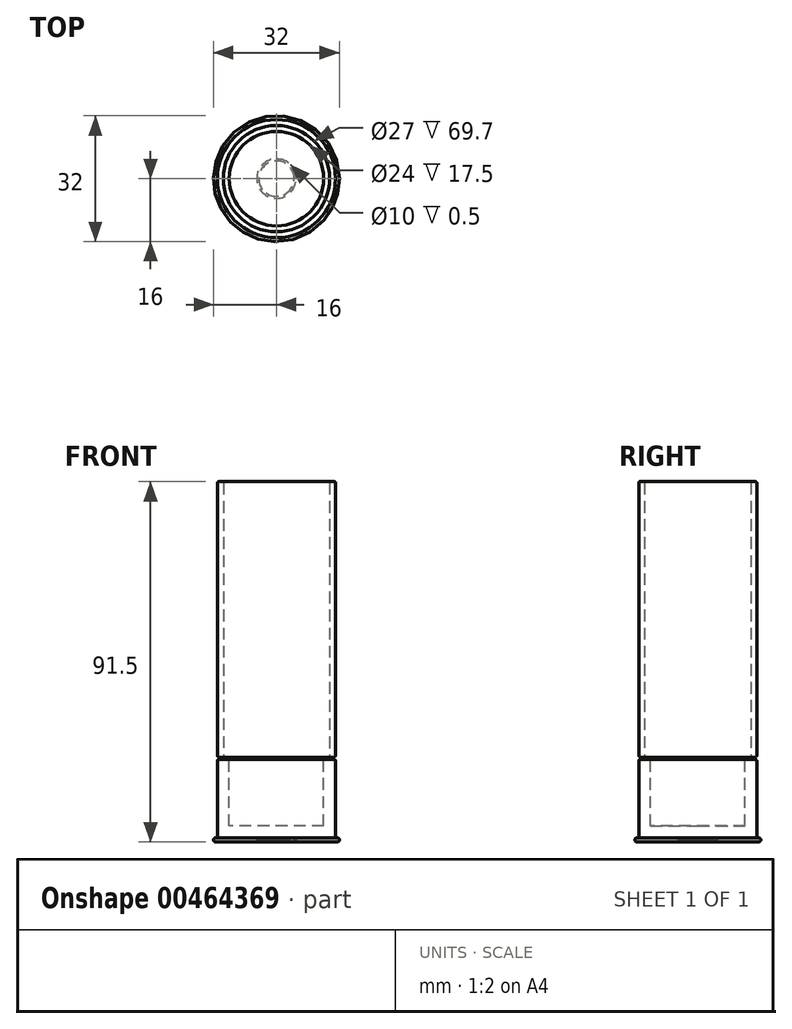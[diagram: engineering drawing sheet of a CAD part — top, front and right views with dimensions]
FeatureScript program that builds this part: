
annotation { "Feature Type Name" : "Feature", "Feature Type Description" : "" }
export const myFeature = defineFeature(function(context is Context, id is Id, definition is map)
    precondition{}
    {
        {
            var Q0;
            Q0=qCreatedBy(makeId("Top.planeOp"),FACE);
            var sketch = newSketch(context, id + "F0", { "sketchPlane" : qUnion([Q0])});
            skCircle(sketch, "E0", {"center": v(0, 0) * mm, "radius": 16 * mm});
            skSolve(sketch);
        }
        {
            var Q0;
            Q0 = qSketchRegion(id + "F0", true);
            extrude(context, id + "F1", {"entities" : qUnion([Q0]), "depth" : 1 * mm});
        }
        {
            var Q0;
            Q0=makeQuery(id+"F1.opExtrude","CAP_FACE",FACE,{"disambiguationData":[OSD([sQuery(id+"F0.wireOp",EDGE,"E0")])],"isStart":false});
            var sketch = newSketch(context, id + "F2", { "sketchPlane" : qUnion([Q0])});
            skCircle(sketch, "E1", {"center": v(0, 0) * mm, "radius": 15 * mm});
            skSolve(sketch);
        }
        {
            var Q0;
            Q0 = qSketchRegion(id + "F2", true);
            extrude(context, id + "F3", {"entities" : qUnion([Q0]), "operationType" : NewBodyOperationType.ADD, "depth" : 20 * mm});
        }
        {
            var Q0;
            Q0=makeQuery(id+"F3.opExtrude","CAP_FACE",FACE,{"disambiguationData":[OSD([sQuery(id+"F2.wireOp",EDGE,"E1")])],"isStart":false});
            var sketch = newSketch(context, id + "F4", { "sketchPlane" : qUnion([Q0])});
            skCircle(sketch, "E2", {"center": v(0, 0) * mm, "radius": 12 * mm});
            skSolve(sketch);
        }
        {
            var Q0;
            Q0 = qSketchRegion(id + "F4", true);
            extrude(context, id + "F5", {"entities" : qUnion([Q0]), "operationType" : NewBodyOperationType.REMOVE, "oppositeDirection" : true, "depth" : 17 * mm});
        }
        {
            var Q0;
            Q0=makeQuery(id+"F3.opExtrude","CAP_FACE",FACE,{"disambiguationData":[OSD([sQuery(id+"F2.wireOp",EDGE,"E1")])],"isStart":false});
            var sketch = newSketch(context, id + "F6", { "sketchPlane" : qUnion([Q0])});
            skCircle(sketch, "E3", {"center": v(0, 0) * mm, "radius": 13.5 * mm});
            skCircle(sketch, "E4", {"center": v(0, 0) * mm, "radius": 12 * mm});
            skSolve(sketch);
        }
        {
            var Q0;
            Q0 = qSketchRegion(id + "F6", true);
            extrude(context, id + "F7", {"entities" : qUnion([Q0]), "operationType" : NewBodyOperationType.ADD, "depth" : .5 * mm});
        }
        {
            var Q0;
            Q0=makeQuery(id+"F7.opExtrude","CAP_FACE",FACE,{"disambiguationData":[OSD([sQuery(id+"F6.wireOp",EDGE,"E3"),sQuery(id+"F6.wireOp",EDGE,"E4")])],"isStart":false});
            var sketch = newSketch(context, id + "F8", { "sketchPlane" : qUnion([Q0])});
            skCircle(sketch, "E5", {"center": v(0, 0) * mm, "radius": 15 * mm});
            skCircle(sketch, "E6", {"center": v(0, 0) * mm, "radius": 13.5 * mm});
            skSolve(sketch);
        }
        {
            var Q0;
            Q0 = qSketchRegion(id + "F8", true);
            extrude(context, id + "F9", {"entities" : qUnion([Q0]), "depth" : 70 * mm});
        }
        {
            var Q0;
            Q0=makeQuery(id+"F9.opExtrude","CAP_EDGE",EDGE,{"disambiguationData":[OSD([sQuery(id+"F8.wireOp",EDGE,"E5")])],"isStart":true});
            var Q1;
            Q1=makeQuery(id+"F3.opExtrude","CAP_EDGE",EDGE,{"disambiguationData":[OSD([sQuery(id+"F2.wireOp",EDGE,"E1")])],"isStart":false});
            fillet(context, id + "F10", {"entities" : qUnion([Q0, Q1]), "radius" : .5 * mm, "tangentPropagation" : true, "allowEdgeOverflow" : false});
        }
        {
            var Q0;
            Q0=makeQuery(id+"F1.opExtrude","CAP_EDGE",EDGE,{"disambiguationData":[OSD([sQuery(id+"F0.wireOp",EDGE,"E0")])],"isStart":false});
            var Q1;
            Q1=makeQuery(id+"F1.opExtrude","CAP_EDGE",EDGE,{"disambiguationData":[OSD([sQuery(id+"F0.wireOp",EDGE,"E0")])],"isStart":true});
            fillet(context, id + "F11", {"entities" : qUnion([Q0, Q1]), "radius" : .5 * mm, "tangentPropagation" : true, "allowEdgeOverflow" : false});
        }
        {
            var Q0;
            Q0=makeQuery(id+"F9.opExtrude","CAP_EDGE",EDGE,{"disambiguationData":[OSD([sQuery(id+"F8.wireOp",EDGE,"E6")])],"isStart":false});
            var Q1;
            Q1=makeQuery(id+"F9.opExtrude","CAP_EDGE",EDGE,{"disambiguationData":[OSD([sQuery(id+"F8.wireOp",EDGE,"E5")])],"isStart":false});
            fillet(context, id + "F12", {"entities" : qUnion([Q0, Q1]), "radius" : .3 * mm, "tangentPropagation" : true, "allowEdgeOverflow" : false});
        }
        {
            var Q0;
            Q0=makeQuery(id+"F1.opExtrude","CAP_FACE",FACE,{"disambiguationData":[OSD([sQuery(id+"F0.wireOp",EDGE,"E0")])],"isStart":true});
            var sketch = newSketch(context, id + "F13", { "sketchPlane" : qUnion([Q0])});
            skCircle(sketch, "E7", {"center": v(0, 0) * mm, "radius": 5 * mm});
            skCircle(sketch, "E8", {"center": v(0, 0) * mm, "radius": 4.5 * mm});
            skCircle(sketch, "E9", {"center": v(0, 0) * mm, "radius": 3.5 * mm});
            skCircle(sketch, "E10", {"center": v(0, 0) * mm, "radius": 2.5 * mm});
            skSolve(sketch);
        }
        {
            var Q0;
            Q0 = qSketchRegion(id + "F13", true);
            var Q1;
            Q1=makeQuery(id+"F13.imprint","IMPRINT",FACE,{"disambiguationData":[TD([[makeQuery(id+"F13.imprint","IMPRINT",EDGE,{"derivedFrom":sQuery(id+"F13.wireOp",EDGE,"E9")}),1.0]])]});
            extrude(context, id + "F14", {"entities" : qUnion([Q0, Q1]), "operationType" : NewBodyOperationType.REMOVE, "oppositeDirection" : true, "depth" : .5 * mm});
        }
        {
            var Q0;
            Q0=makeQuery(id+"F14.boolean.opBoolean","COPY",EDGE,{"derivedFrom":makeQuery(id+"F14.opExtrude","CAP_EDGE",EDGE,{"disambiguationData":[OSD([sQuery(id+"F13.wireOp",EDGE,"E9")])],"isStart":true})});
            var Q1;
            Q1=makeQuery(id+"F14.boolean.opBoolean","COPY",EDGE,{"derivedFrom":makeQuery(id+"F14.opExtrude","CAP_EDGE",EDGE,{"disambiguationData":[OSD([sQuery(id+"F13.wireOp",EDGE,"E7")])],"isStart":true})});
            fillet(context, id + "F15", {"entities" : qUnion([Q0, Q1]), "radius" : .5 * mm, "tangentPropagation" : true, "allowEdgeOverflow" : false});
        }
        {
            var Q0;
            Q0=makeQuery(id+"F14.boolean.opBoolean","COPY",EDGE,{"derivedFrom":makeQuery(id+"F14.opExtrude","CAP_EDGE",EDGE,{"disambiguationData":[OSD([sQuery(id+"F13.wireOp",EDGE,"E8")])],"isStart":true})});
            fillet(context, id + "F16", {"entities" : qUnion([Q0]), "radius" : .1 * mm, "tangentPropagation" : true, "allowEdgeOverflow" : false});
        }
        {
            var Q0;
            Q0=makeQuery(id+"F14.boolean.opBoolean","COPY",EDGE,{"derivedFrom":makeQuery(id+"F14.opExtrude","CAP_EDGE",EDGE,{"disambiguationData":[OSD([sQuery(id+"F13.wireOp",EDGE,"E10")])],"isStart":true})});
            fillet(context, id + "F17", {"entities" : qUnion([Q0]), "radius" : .9 * mm, "tangentPropagation" : true, "allowEdgeOverflow" : false});
        }
        {
            var Q0;
            {var subQ0=sQuery(id+"F13.wireOp",EDGE,"E9");Q0=makeQuery(id+"F15.opFillet","BLEND_EDGE",EDGE,{"blendedFrom":[makeQuery(id+"F14.boolean.opBoolean","COPY",EDGE,{"derivedFrom":makeQuery(id+"F14.opExtrude","CAP_EDGE",EDGE,{"disambiguationData":[OSD([subQ0])],"isStart":true})}),makeQuery(id+"F14.boolean.opBoolean","COPY",FACE,{"derivedFrom":makeQuery(id+"F14.opExtrude","CAP_FACE",FACE,{"disambiguationData":[OSD([subQ0,sQuery(id+"F13.wireOp",EDGE,"E10")])],"isStart":false})})],"blendedInto":[makeQuery(id+"F14.boolean.opBoolean","COPY",FACE,{"derivedFrom":makeQuery(id+"F14.opExtrude","CAP_FACE",FACE,{"disambiguationData":[OSD([subQ0,sQuery(id+"F13.wireOp",EDGE,"E10")])],"isStart":false})})]});}
            var Q1;
            {var subQ0=sQuery(id+"F13.wireOp",EDGE,"E10");Q1=makeQuery(id+"F17.opFillet","BLEND_EDGE",EDGE,{"blendedFrom":[makeQuery(id+"F14.boolean.opBoolean","COPY",EDGE,{"derivedFrom":makeQuery(id+"F14.opExtrude","CAP_EDGE",EDGE,{"disambiguationData":[OSD([subQ0])],"isStart":true})}),makeQuery(id+"F14.boolean.opBoolean","COPY",FACE,{"derivedFrom":makeQuery(id+"F14.opExtrude","CAP_FACE",FACE,{"disambiguationData":[OSD([sQuery(id+"F13.wireOp",EDGE,"E9"),subQ0])],"isStart":false})})],"blendedInto":[makeQuery(id+"F14.boolean.opBoolean","COPY",FACE,{"derivedFrom":makeQuery(id+"F14.opExtrude","CAP_FACE",FACE,{"disambiguationData":[OSD([sQuery(id+"F13.wireOp",EDGE,"E9"),subQ0])],"isStart":false})})]});}
            fillet(context, id + "F18", {"entities" : qUnion([Q0, Q1]), "radius" : .4 * mm, "tangentPropagation" : true, "allowEdgeOverflow" : false});
        }
    });
